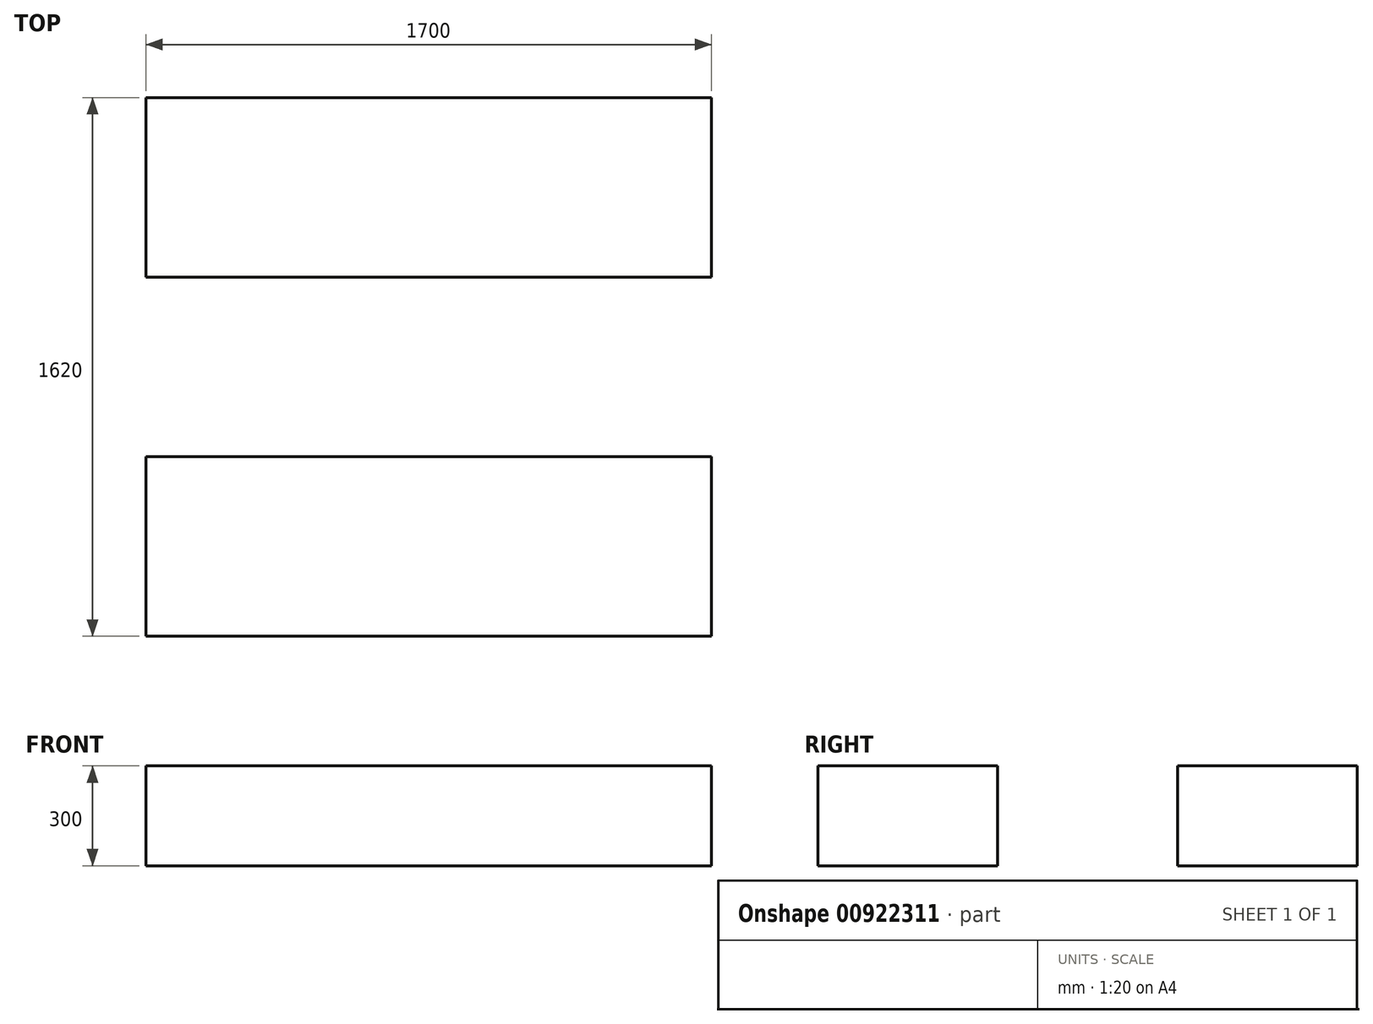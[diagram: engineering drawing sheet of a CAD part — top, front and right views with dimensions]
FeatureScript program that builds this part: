
annotation { "Feature Type Name" : "Feature", "Feature Type Description" : "" }
export const myFeature = defineFeature(function(context is Context, id is Id, definition is map)
    precondition{}
    {
        {
            var Q0;
            Q0=qCreatedBy(makeId("Top.planeOp"),FACE);
            var sketch = newSketch(context, id + "F0", { "sketchPlane" : qUnion([Q0])});
            skLineSegment(sketch, "E0", {"start": v(0, 0) * mm, "end": v(-1700, 0) * mm});
            skLineSegment(sketch, "E1", {"start": v(-1700, 0) * mm, "end": v(-1700, 540) * mm});
            skLineSegment(sketch, "E2", {"start": v(-1700, 540) * mm, "end": v(0, 540) * mm});
            skLineSegment(sketch, "E3", {"start": v(0, 540) * mm, "end": v(0, 0) * mm});
            skLineSegment(sketch, "E4", {"start": v(0, 0) * mm, "end": v(0, 150) * mm});
            skLineSegment(sketch, "E5", {"start": v(0, 150) * mm, "end": v(-1700, 150) * mm});
            skLineSegment(sketch, "E6", {"start": v(-1700, 150) * mm, "end": v(-1700, 0) * mm});
            skLineSegment(sketch, "E7", {"start": v(0, 540) * mm, "end": v(0, 1080) * mm});
            skLineSegment(sketch, "E8", {"start": v(0, 1080) * mm, "end": v(-540, 1080) * mm});
            skLineSegment(sketch, "E9", {"start": v(-540, 1080) * mm, "end": v(-540, 540) * mm});
            skLineSegment(sketch, "E10", {"start": v(-540, 540) * mm, "end": v(0, 540) * mm});
            skLineSegment(sketch, "E11", {"start": v(0, 1080) * mm, "end": v(-1700, 1080) * mm});
            skLineSegment(sketch, "E12", {"start": v(-1700, 1080) * mm, "end": v(-1700, 1620) * mm});
            skLineSegment(sketch, "E13", {"start": v(-1700, 1620) * mm, "end": v(0, 1620) * mm});
            skLineSegment(sketch, "E14", {"start": v(0, 1620) * mm, "end": v(0, 1080) * mm});
            skLineSegment(sketch, "E15", {"start": v(0, 1620) * mm, "end": v(0, 1470) * mm});
            skLineSegment(sketch, "E16", {"start": v(0, 1470) * mm, "end": v(-1700, 1470) * mm});
            skLineSegment(sketch, "E17", {"start": v(-1700, 1470) * mm, "end": v(-1700, 1620) * mm});
            skSolve(sketch);
        }
        {
            var Q0;
            {var subQ3=sQuery(id+"F0.wireOp",EDGE,"E5");Q0=makeQuery(id+"F0.imprint","IMPRINT",FACE,{"disambiguationData":[TD([[makeQuery(id+"F0.imprint","IMPRINT",EDGE,{"derivedFrom":subQ3}),-1.0]])]});}
            var Q1;
            {var subQ0=sQuery(id+"F0.wireOp",EDGE,"E0");Q1=makeQuery(id+"F0.imprint","IMPRINT",FACE,{"disambiguationData":[TD([[makeQuery(id+"F0.imprint","IMPRINT",EDGE,{"derivedFrom":subQ0}),-1.0]])]});}
            var Q2;
            {var subQ1=sQuery(id+"F0.wireOp",EDGE,"E8");Q2=makeQuery(id+"F0.imprint","IMPRINT",FACE,{"disambiguationData":[TD([[makeQuery(id+"F0.imprint","IMPRINT",EDGE,{"derivedFrom":subQ1}),-1.0]])]});}
            var Q3;
            {var subQ0=sQuery(id+"F0.wireOp",EDGE,"E13");Q3=makeQuery(id+"F0.imprint","IMPRINT",FACE,{"disambiguationData":[TD([[makeQuery(id+"F0.imprint","IMPRINT",EDGE,{"derivedFrom":subQ0}),-1.0]])]});}
            extrude(context, id + "F1", {"entities" : qUnion([Q0, Q1, Q2, Q3]), "oppositeDirection" : true, "depth" : 300 * mm, "offsetDistance" : 25 * mm});
        }
    });
